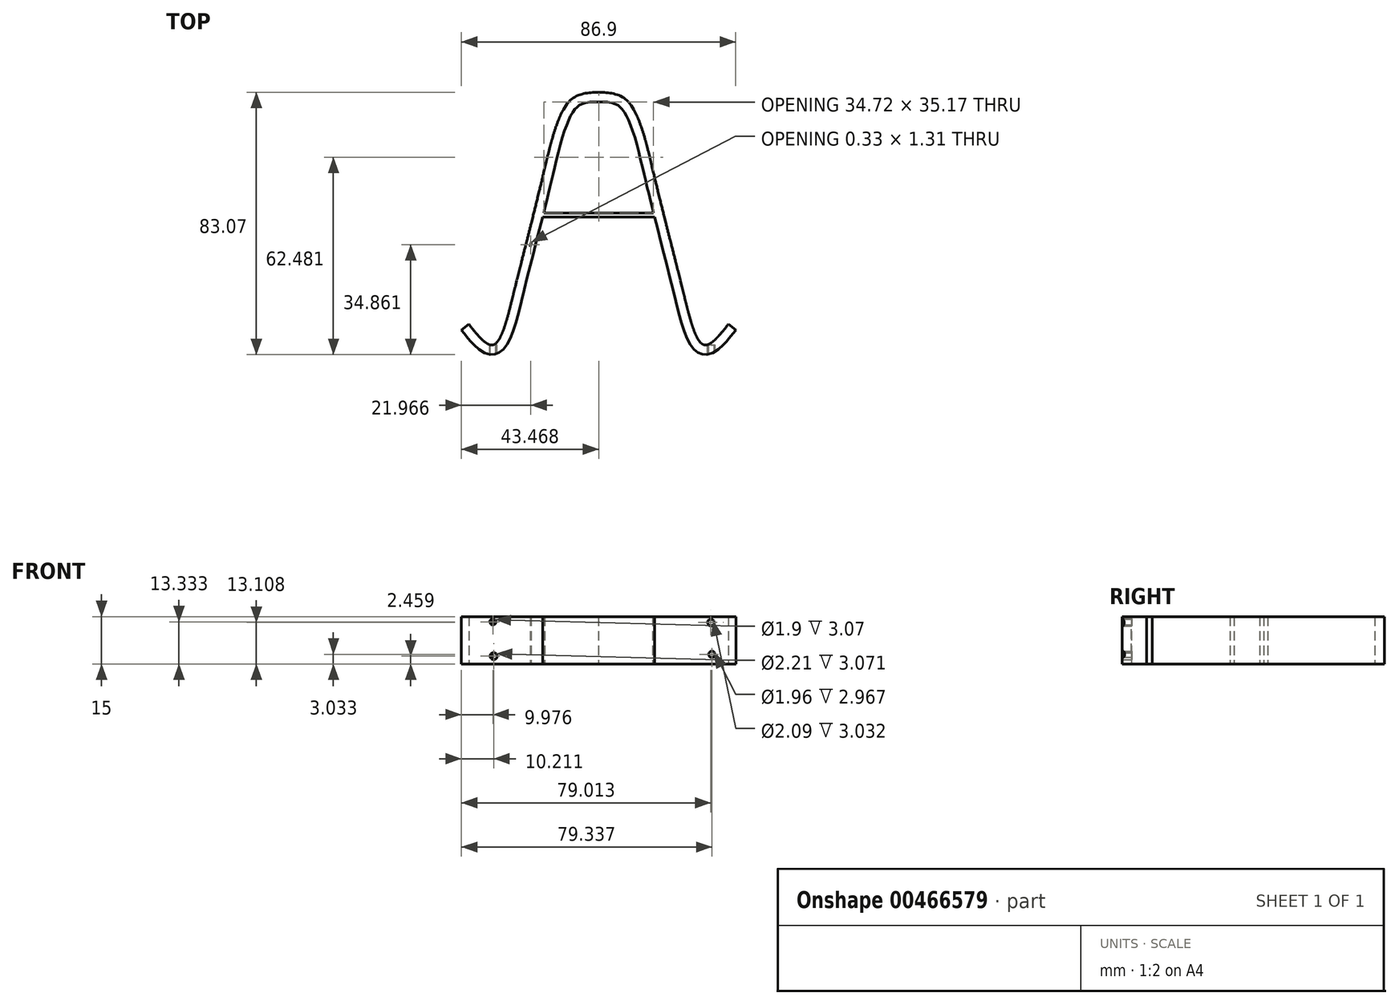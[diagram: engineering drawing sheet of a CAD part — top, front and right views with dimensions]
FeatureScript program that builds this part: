
annotation { "Feature Type Name" : "Feature", "Feature Type Description" : "" }
export const myFeature = defineFeature(function(context is Context, id is Id, definition is map)
    precondition{}
    {
        {
            var Q0;
            Q0=qCreatedBy(makeId("Top.planeOp"),FACE);
            var sketch = newSketch(context, id + "F0", { "sketchPlane" : qUnion([Q0])});
            skPoint(sketch, "E0", {"position": v(-40, 0) * mm});
            skPoint(sketch, "E1", {"position": v(40, 0) * mm});
            skPoint(sketch, "E2", {"position": v(0, 80) * mm});
            skFitSpline(sketch, "E3", {"points": [v(-41.08, 6.55) * mm, v(-38.1, 2.93) * mm, v(-33.42, 0) * mm, v(-26.81, 16.77) * mm, v(-17.66, 53.4) * mm, v(-8.92, 77.47) * mm, v(0, 80) * mm], "startDerivative": vector(27.62, -35.66) * mm, "endDerivative": vector(72.84, 2.27) * mm});
            skFitSpline(sketch, "E4.MirrorCS", {"points": [v(41.08, 6.55) * mm, v(38.1, 2.93) * mm, v(33.42, 0) * mm, v(26.81, 16.77) * mm, v(17.66, 53.4) * mm, v(8.92, 77.47) * mm, v(0, 80) * mm], "startDerivative": vector(-27.62, -35.66) * mm, "endDerivative": vector(-72.84, 2.27) * mm});
            skFitSpline(sketch, "E5.0", {"points": [v(-43.45, 4.7) * mm, v(-43.17, 4.34) * mm, v(-42.72, 3.77) * mm, v(-42.08, 2.96) * mm, v(-41.55, 2.32) * mm, v(-41.08, 1.76) * mm, v(-40.67, 1.3) * mm, v(-40.35, 0.93) * mm, v(-40, 0.56) * mm, v(-39.51, 0.04) * mm, v(-38.84, -0.64) * mm, v(-37.91, -1.45) * mm, v(-36.84, -2.2) * mm, v(-35.75, -2.74) * mm, v(-34.67, -3) * mm, v(-33.92, -3.07) * mm, v(-33.28, -3.03) * mm, v(-32.79, -2.94) * mm, v(-32.3, -2.8) * mm, v(-31.7, -2.57) * mm, v(-31.05, -2.18) * mm, v(-30.4, -1.65) * mm, v(-29.84, -1.07) * mm, v(-29.21, -0.25) * mm, v(-28.55, 0.83) * mm, v(-27.88, 2.26) * mm, v(-27.26, 3.82) * mm, v(-26.7, 5.5) * mm, v(-25.96, 7.91) * mm, v(-25.1, 11.16) * mm, v(-24.1, 15.28) * mm, v(-23.06, 19.44) * mm, v(-22, 23.66) * mm, v(-20.92, 27.91) * mm, v(-19.83, 32.2) * mm, v(-18.74, 36.51) * mm, v(-17.64, 40.85) * mm, v(-16.56, 45.2) * mm, v(-15.67, 48.82) * mm, v(-14.97, 51.71) * mm, v(-14.28, 54.6) * mm, v(-13.44, 58.18) * mm, v(-12.42, 62.28) * mm, v(-11.36, 66.07) * mm, v(-10.42, 68.88) * mm, v(-9.63, 70.85) * mm, v(-9.02, 72.17) * mm, v(-8.4, 73.31) * mm, v(-7.78, 74.26) * mm, v(-7.27, 74.88) * mm, v(-6.89, 75.27) * mm, v(-6.52, 75.6) * mm, v(-6.03, 75.93) * mm, v(-5.4, 76.25) * mm, v(-4.7, 76.5) * mm, v(-3.65, 76.75) * mm, v(-2.1, 76.93) * mm, v(-0.67, 76.98) * mm, v(0.1, 77) * mm]});
            skFitSpline(sketch, "E6.0", {"points": [v(43.45, 4.7) * mm, v(43.17, 4.34) * mm, v(42.72, 3.77) * mm, v(42.08, 2.96) * mm, v(41.55, 2.32) * mm, v(41.08, 1.76) * mm, v(40.67, 1.3) * mm, v(40.35, 0.93) * mm, v(40, 0.56) * mm, v(39.51, 0.04) * mm, v(38.84, -0.64) * mm, v(37.91, -1.45) * mm, v(36.84, -2.2) * mm, v(35.75, -2.74) * mm, v(34.67, -3) * mm, v(33.92, -3.07) * mm, v(33.28, -3.03) * mm, v(32.79, -2.94) * mm, v(32.3, -2.8) * mm, v(31.7, -2.57) * mm, v(31.05, -2.18) * mm, v(30.4, -1.65) * mm, v(29.84, -1.07) * mm, v(29.21, -0.25) * mm, v(28.55, 0.83) * mm, v(27.88, 2.26) * mm, v(27.26, 3.82) * mm, v(26.7, 5.5) * mm, v(25.96, 7.91) * mm, v(25.1, 11.16) * mm, v(24.1, 15.28) * mm, v(23.06, 19.44) * mm, v(22, 23.66) * mm, v(20.92, 27.91) * mm, v(19.83, 32.2) * mm, v(18.74, 36.51) * mm, v(17.64, 40.85) * mm, v(16.56, 45.2) * mm, v(15.67, 48.82) * mm, v(14.97, 51.71) * mm, v(14.28, 54.6) * mm, v(13.44, 58.18) * mm, v(12.42, 62.28) * mm, v(11.36, 66.07) * mm, v(10.42, 68.88) * mm, v(9.63, 70.85) * mm, v(9.02, 72.17) * mm, v(8.4, 73.31) * mm, v(7.78, 74.26) * mm, v(7.27, 74.88) * mm, v(6.89, 75.27) * mm, v(6.52, 75.6) * mm, v(6.03, 75.93) * mm, v(5.4, 76.25) * mm, v(4.7, 76.5) * mm, v(3.65, 76.75) * mm, v(2.1, 76.93) * mm, v(0.67, 76.98) * mm, v(-0.1, 77) * mm]});
            skLineSegment(sketch, "E7", {"start": v(-43.45, 4.7) * mm, "end": v(-41.08, 6.55) * mm});
            skLineSegment(sketch, "E8", {"start": v(43.45, 4.7) * mm, "end": v(41.08, 6.55) * mm});
            skLineSegment(sketch, "E9", {"start": v(-17.08, 43.11) * mm, "end": v(17.08, 43.11) * mm});
            skLineSegment(sketch, "E10", {"start": v(-17.73, 40.51) * mm, "end": v(17.73, 40.51) * mm});
            skFitSpline(sketch, "E11.trimOffspring", {"points": [v(-43.45, 4.7) * mm, v(-43.17, 4.34) * mm, v(-42.72, 3.77) * mm, v(-42.08, 2.96) * mm, v(-41.55, 2.32) * mm, v(-41.08, 1.76) * mm, v(-40.67, 1.3) * mm, v(-40.35, 0.93) * mm, v(-40, 0.56) * mm, v(-39.51, 0.04) * mm, v(-38.84, -0.64) * mm, v(-37.91, -1.45) * mm, v(-36.84, -2.2) * mm, v(-35.75, -2.74) * mm, v(-34.67, -3) * mm, v(-33.92, -3.07) * mm, v(-33.28, -3.03) * mm, v(-32.79, -2.94) * mm, v(-32.3, -2.8) * mm, v(-31.7, -2.57) * mm, v(-31.05, -2.18) * mm, v(-30.4, -1.65) * mm, v(-29.84, -1.07) * mm, v(-29.21, -0.25) * mm, v(-28.55, 0.83) * mm, v(-27.88, 2.26) * mm, v(-27.26, 3.82) * mm, v(-26.7, 5.5) * mm, v(-25.96, 7.91) * mm, v(-25.1, 11.16) * mm, v(-24.1, 15.28) * mm, v(-23.06, 19.44) * mm, v(-22, 23.66) * mm, v(-20.92, 27.91) * mm, v(-19.83, 32.2) * mm, v(-18.74, 36.51) * mm, v(-17.64, 40.85) * mm, v(-16.56, 45.2) * mm, v(-15.67, 48.82) * mm, v(-14.97, 51.71) * mm, v(-14.28, 54.6) * mm, v(-13.44, 58.18) * mm, v(-12.42, 62.28) * mm, v(-11.36, 66.07) * mm, v(-10.42, 68.88) * mm, v(-9.63, 70.85) * mm, v(-9.02, 72.17) * mm, v(-8.4, 73.31) * mm, v(-7.78, 74.26) * mm, v(-7.27, 74.88) * mm, v(-6.89, 75.27) * mm, v(-6.52, 75.6) * mm, v(-6.03, 75.93) * mm, v(-5.4, 76.25) * mm, v(-4.7, 76.5) * mm, v(-3.65, 76.75) * mm, v(-2.1, 76.93) * mm, v(-0.67, 76.98) * mm, v(0.1, 77) * mm]});
            skFitSpline(sketch, "E12.trimOffspring", {"points": [v(43.45, 4.7) * mm, v(43.17, 4.34) * mm, v(42.72, 3.77) * mm, v(42.08, 2.96) * mm, v(41.55, 2.32) * mm, v(41.08, 1.76) * mm, v(40.67, 1.3) * mm, v(40.35, 0.93) * mm, v(40, 0.56) * mm, v(39.51, 0.04) * mm, v(38.84, -0.64) * mm, v(37.91, -1.45) * mm, v(36.84, -2.2) * mm, v(35.75, -2.74) * mm, v(34.67, -3) * mm, v(33.92, -3.07) * mm, v(33.28, -3.03) * mm, v(32.79, -2.94) * mm, v(32.3, -2.8) * mm, v(31.7, -2.57) * mm, v(31.05, -2.18) * mm, v(30.4, -1.65) * mm, v(29.84, -1.07) * mm, v(29.21, -0.25) * mm, v(28.55, 0.83) * mm, v(27.88, 2.26) * mm, v(27.26, 3.82) * mm, v(26.7, 5.5) * mm, v(25.96, 7.91) * mm, v(25.1, 11.16) * mm, v(24.1, 15.28) * mm, v(23.06, 19.44) * mm, v(22, 23.66) * mm, v(20.92, 27.91) * mm, v(19.83, 32.2) * mm, v(18.74, 36.51) * mm, v(17.64, 40.85) * mm, v(16.56, 45.2) * mm, v(15.67, 48.82) * mm, v(14.97, 51.71) * mm, v(14.28, 54.6) * mm, v(13.44, 58.18) * mm, v(12.42, 62.28) * mm, v(11.36, 66.07) * mm, v(10.42, 68.88) * mm, v(9.63, 70.85) * mm, v(9.02, 72.17) * mm, v(8.4, 73.31) * mm, v(7.78, 74.26) * mm, v(7.27, 74.88) * mm, v(6.89, 75.27) * mm, v(6.52, 75.6) * mm, v(6.03, 75.93) * mm, v(5.4, 76.25) * mm, v(4.7, 76.5) * mm, v(3.65, 76.75) * mm, v(2.1, 76.93) * mm, v(0.67, 76.98) * mm, v(-0.1, 77) * mm]});
            skFitSpline(sketch, "E13.0", {"points": [v(-42.27, 5.63) * mm, v(-41.98, 5.26) * mm, v(-41.54, 4.7) * mm, v(-40.91, 3.9) * mm, v(-40.4, 3.28) * mm, v(-39.85, 2.63) * mm, v(-39.24, 1.95) * mm, v(-38.56, 1.2) * mm, v(-37.8, 0.45) * mm, v(-36.98, -0.28) * mm, v(-36.07, -0.91) * mm, v(-35.2, -1.33) * mm, v(-34.42, -1.52) * mm, v(-33.79, -1.57) * mm, v(-33.23, -1.51) * mm, v(-32.8, -1.38) * mm, v(-32.38, -1.22) * mm, v(-31.91, -0.95) * mm, v(-31.26, -0.41) * mm, v(-30.58, 0.4) * mm, v(-29.88, 1.53) * mm, v(-29.26, 2.85) * mm, v(-28.67, 4.33) * mm, v(-28.12, 5.96) * mm, v(-27.41, 8.31) * mm, v(-26.56, 11.53) * mm, v(-25.55, 15.64) * mm, v(-24.52, 19.8) * mm, v(-23.46, 24.03) * mm, v(-22.38, 28.28) * mm, v(-20.92, 34) * mm, v(-19.46, 39.77) * mm, v(-18.02, 45.55) * mm, v(-17.13, 49.17) * mm, v(-16.43, 52.06) * mm, v(-15.74, 54.95) * mm, v(-14.9, 58.53) * mm, v(-13.87, 62.65) * mm, v(-12.8, 66.5) * mm, v(-11.64, 69.96) * mm, v(-10.6, 72.42) * mm, v(-9.7, 74.07) * mm, v(-9, 75.14) * mm, v(-8.28, 76.02) * mm, v(-7.56, 76.7) * mm, v(-6.8, 77.22) * mm, v(-5.72, 77.77) * mm, v(-4.23, 78.2) * mm, v(-2.2, 78.43) * mm, v(-0.71, 78.48) * mm, v(0.05, 78.5) * mm]});
            skFitSpline(sketch, "E14.0", {"points": [v(42.27, 5.63) * mm, v(41.98, 5.26) * mm, v(41.54, 4.7) * mm, v(40.91, 3.9) * mm, v(40.4, 3.28) * mm, v(39.85, 2.63) * mm, v(39.24, 1.95) * mm, v(38.56, 1.2) * mm, v(37.8, 0.45) * mm, v(36.98, -0.28) * mm, v(36.07, -0.91) * mm, v(35.2, -1.33) * mm, v(34.42, -1.52) * mm, v(33.79, -1.57) * mm, v(33.23, -1.51) * mm, v(32.8, -1.38) * mm, v(32.38, -1.22) * mm, v(31.91, -0.95) * mm, v(31.26, -0.41) * mm, v(30.58, 0.4) * mm, v(29.88, 1.53) * mm, v(29.26, 2.85) * mm, v(28.67, 4.33) * mm, v(28.12, 5.96) * mm, v(27.41, 8.31) * mm, v(26.56, 11.53) * mm, v(25.55, 15.64) * mm, v(24.52, 19.8) * mm, v(23.46, 24.03) * mm, v(22.38, 28.28) * mm, v(20.92, 34) * mm, v(19.46, 39.77) * mm, v(18.02, 45.55) * mm, v(17.13, 49.17) * mm, v(16.43, 52.06) * mm, v(15.74, 54.95) * mm, v(14.9, 58.53) * mm, v(13.87, 62.65) * mm, v(12.8, 66.5) * mm, v(11.64, 69.96) * mm, v(10.6, 72.42) * mm, v(9.7, 74.07) * mm, v(9, 75.14) * mm, v(8.28, 76.02) * mm, v(7.56, 76.7) * mm, v(6.8, 77.22) * mm, v(5.72, 77.77) * mm, v(4.23, 78.2) * mm, v(2.2, 78.43) * mm, v(0.71, 78.48) * mm, v(-0.05, 78.5) * mm]});
            skLineSegment(sketch, "E15", {"start": v(-17.34, 41.82) * mm, "end": v(17.38, 41.82) * mm});
            skLineSegment(sketch, "E16", {"start": v(-17.34, 41.82) * mm, "end": v(-17.08, 43.11) * mm});
            skLineSegment(sketch, "E17", {"start": v(17.38, 41.82) * mm, "end": v(17.08, 43.11) * mm});
            skLineSegment(sketch, "E18", {"start": v(-41.43, 4.56) * mm, "end": v(-40.22, 5.43) * mm});
            skLineSegment(sketch, "E19", {"start": v(-39.27, 1.98) * mm, "end": v(-38.1, 2.93) * mm});
            skLineSegment(sketch, "E20", {"start": v(-38.36, 1) * mm, "end": v(-37.3, 2.06) * mm});
            skLineSegment(sketch, "E21", {"start": v(-35.26, 0.39) * mm, "end": v(-35.26, -1.27) * mm});
            skLineSegment(sketch, "E22", {"start": v(-33.88, -0.05) * mm, "end": v(-33.88, -1.55) * mm});
            skLineSegment(sketch, "E23", {"start": v(-31.9, 1.18) * mm, "end": v(-30.54, 0.5) * mm});
            skLineSegment(sketch, "E24", {"start": v(-30.54, 0.5) * mm, "end": v(-30.58, 0.53) * mm});
            skLineSegment(sketch, "E25", {"start": v(-31.16, 2.38) * mm, "end": v(-29.77, 1.8) * mm});
            skLineSegment(sketch, "E26", {"start": v(-29.77, 5.78) * mm, "end": v(-28.42, 5.1) * mm});
            skLineSegment(sketch, "E27", {"start": v(-29.26, 7.4) * mm, "end": v(-27.85, 6.85) * mm});
            skLineSegment(sketch, "E28", {"start": v(-28.1, 11.56) * mm, "end": v(-26.72, 10.96) * mm});
            skLineSegment(sketch, "E29", {"start": v(-27.73, 13.05) * mm, "end": v(-26.34, 12.42) * mm});
            skLineSegment(sketch, "E30", {"start": v(-26.37, 18.58) * mm, "end": v(-24.97, 17.95) * mm});
            skLineSegment(sketch, "E31", {"start": v(-25.89, 20.49) * mm, "end": v(-24.47, 20) * mm});
            skLineSegment(sketch, "E32", {"start": v(-24.84, 24.66) * mm, "end": v(-23.45, 24.04) * mm});
            skLineSegment(sketch, "E33", {"start": v(-24.47, 26.14) * mm, "end": v(-23.08, 25.51) * mm});
            skLineSegment(sketch, "E34", {"start": v(-23.08, 25.51) * mm, "end": v(-22.95, 25.96) * mm});
            skLineSegment(sketch, "E35.MirrorCS", {"start": v(41.43, 4.56) * mm, "end": v(40.22, 5.43) * mm});
            skLineSegment(sketch, "E36.MirrorCS", {"start": v(39.27, 1.98) * mm, "end": v(38.1, 2.93) * mm});
            skLineSegment(sketch, "E37.MirrorCS", {"start": v(38.36, 1) * mm, "end": v(37.3, 2.06) * mm});
            skLineSegment(sketch, "E38.MirrorCS", {"start": v(35.26, 0.39) * mm, "end": v(35.26, -1.27) * mm});
            skLineSegment(sketch, "E39.MirrorCS", {"start": v(33.88, -0.05) * mm, "end": v(33.88, -1.55) * mm});
            skLineSegment(sketch, "E40.MirrorCS", {"start": v(31.9, 1.18) * mm, "end": v(30.54, 0.5) * mm});
            skLineSegment(sketch, "E41.MirrorCS", {"start": v(31.16, 2.38) * mm, "end": v(29.77, 1.8) * mm});
            skLineSegment(sketch, "E42.MirrorCS", {"start": v(29.77, 5.78) * mm, "end": v(28.42, 5.1) * mm});
            skLineSegment(sketch, "E43.MirrorCS", {"start": v(29.26, 7.4) * mm, "end": v(27.85, 6.85) * mm});
            skLineSegment(sketch, "E44.MirrorCS", {"start": v(28.1, 11.56) * mm, "end": v(26.72, 10.96) * mm});
            skLineSegment(sketch, "E45.MirrorCS", {"start": v(27.73, 13.05) * mm, "end": v(26.34, 12.42) * mm});
            skLineSegment(sketch, "E46.MirrorCS", {"start": v(26.37, 18.58) * mm, "end": v(24.97, 17.95) * mm});
            skLineSegment(sketch, "E47.MirrorCS", {"start": v(25.89, 20.49) * mm, "end": v(24.47, 20) * mm});
            skLineSegment(sketch, "E48.MirrorCS", {"start": v(24.47, 26.14) * mm, "end": v(23.08, 25.51) * mm});
            skLineSegment(sketch, "E49.MirrorCS", {"start": v(24.84, 24.66) * mm, "end": v(23.45, 24.04) * mm});
            skLineSegment(sketch, "E50", {"start": v(-23.04, 31.76) * mm, "end": v(-21.65, 31.14) * mm});
            skLineSegment(sketch, "E51", {"start": v(-21.65, 31.14) * mm, "end": v(-21.3, 32.54) * mm});
            skLineSegment(sketch, "E52", {"start": v(-21.3, 32.54) * mm, "end": v(-22.67, 33.23) * mm});
            skLineSegment(sketch, "E53", {"start": v(-21.3, 38.64) * mm, "end": v(-19.84, 38.27) * mm});
            skLineSegment(sketch, "E54", {"start": v(-20.88, 40.28) * mm, "end": v(-19.45, 39.8) * mm});
            skLineSegment(sketch, "E55", {"start": v(-19.3, 46.58) * mm, "end": v(-17.9, 46) * mm});
            skLineSegment(sketch, "E56", {"start": v(-18.8, 48.7) * mm, "end": v(-17.4, 48.1) * mm});
            skLineSegment(sketch, "E57", {"start": v(-17.4, 54.51) * mm, "end": v(-15.99, 53.92) * mm});
            skLineSegment(sketch, "E58", {"start": v(-16.9, 56.58) * mm, "end": v(-15.5, 55.99) * mm});
            skLineSegment(sketch, "E59", {"start": v(-15.36, 62.82) * mm, "end": v(-13.96, 62.24) * mm});
            skLineSegment(sketch, "E60", {"start": v(-14.66, 65.38) * mm, "end": v(-13.27, 64.8) * mm});
            skPoint(sketch, "E60.startSnap0", {"position": v(-14.66, 62.53) * mm});
            skLineSegment(sketch, "E61", {"start": v(-13.27, 64.8) * mm, "end": v(-13.38, 64.48) * mm});
            skLineSegment(sketch, "E62", {"start": v(-12.67, 71.32) * mm, "end": v(-11.4, 70.47) * mm});
            skLineSegment(sketch, "E63", {"start": v(-11.92, 73.04) * mm, "end": v(-10.6, 72.31) * mm});
            skLineSegment(sketch, "E64.MirrorCS", {"start": v(21.3, 32.54) * mm, "end": v(22.67, 33.23) * mm});
            skLineSegment(sketch, "E65.MirrorCS", {"start": v(23.04, 31.76) * mm, "end": v(21.65, 31.14) * mm});
            skLineSegment(sketch, "E66.MirrorCS", {"start": v(21.3, 38.64) * mm, "end": v(19.84, 38.27) * mm});
            skLineSegment(sketch, "E67.MirrorCS", {"start": v(20.88, 40.28) * mm, "end": v(19.45, 39.8) * mm});
            skLineSegment(sketch, "E68.MirrorCS", {"start": v(19.3, 46.58) * mm, "end": v(17.9, 46) * mm});
            skLineSegment(sketch, "E69.MirrorCS", {"start": v(18.8, 48.7) * mm, "end": v(17.4, 48.1) * mm});
            skLineSegment(sketch, "E70.MirrorCS", {"start": v(17.4, 54.51) * mm, "end": v(15.99, 53.92) * mm});
            skLineSegment(sketch, "E71.MirrorCS", {"start": v(16.9, 56.58) * mm, "end": v(15.5, 55.99) * mm});
            skLineSegment(sketch, "E72.MirrorCS", {"start": v(15.36, 62.82) * mm, "end": v(13.96, 62.24) * mm});
            skLineSegment(sketch, "E73.MirrorCS", {"start": v(14.66, 65.38) * mm, "end": v(13.27, 64.8) * mm});
            skLineSegment(sketch, "E74.MirrorCS", {"start": v(12.67, 71.32) * mm, "end": v(11.4, 70.47) * mm});
            skLineSegment(sketch, "E75.MirrorCS", {"start": v(11.92, 73.04) * mm, "end": v(10.6, 72.31) * mm});
            skFitSpline(sketch, "E76.trimOffspring", {"points": [v(41.08, 6.55) * mm, v(38.1, 2.93) * mm, v(33.42, 0) * mm, v(26.81, 16.77) * mm, v(17.66, 53.4) * mm, v(8.92, 77.47) * mm, v(0, 80) * mm], "startDerivative": vector(-27.62, -35.66) * mm, "endDerivative": vector(-72.84, 2.27) * mm});
            skLineSegment(sketch, "E77", {"start": v(41.08, 6.55) * mm, "end": v(40.22, 5.43) * mm});
            skPoint(sketch, "E78.end.orphan", {"position": v(-8.08, 76.2) * mm});
            skPoint(sketch, "E79.end.orphan", {"position": v(-6.97, 77.1) * mm});
            skPoint(sketch, "E79.start.orphan", {"position": v(-7.72, 78.4) * mm});
            skPoint(sketch, "E80.end.orphan", {"position": v(-1.06, 78.46) * mm});
            skPoint(sketch, "E81.MirrorCS.end.orphan", {"position": v(1.06, 78.46) * mm});
            skPoint(sketch, "E82.MirrorCS.end.orphan", {"position": v(6.97, 77.1) * mm});
            skPoint(sketch, "E83.MirrorCS.end.orphan", {"position": v(8.08, 76.2) * mm});
            skPoint(sketch, "E84.trimOffspring.end.orphan", {"position": v(7.72, 78.4) * mm});
            skSolve(sketch);
        }
        {
            var Q0;
            Q0 = qSketchRegion(id + "F0", true);
            extrude(context, id + "F1", {"entities" : qUnion([Q0]), "depth" : 15 * mm});
        }
        {
            var Q0;
            Q0=qCreatedBy(makeId("Front.planeOp"),FACE);
            var sketch = newSketch(context, id + "F2", { "sketchPlane" : qUnion([Q0])});
            skCircle(sketch, "E85", {"center": v(-33.47, 13.33) * mm, "radius": 0.95 * mm});
            skCircle(sketch, "E86", {"center": v(-33.24, 2.46) * mm, "radius": 1.1 * mm});
            skCircle(sketch, "E87", {"center": v(35.56, 13.1) * mm, "radius": 1.05 * mm});
            skCircle(sketch, "E88", {"center": v(35.89, 3.03) * mm, "radius": 0.98 * mm});
            skSolve(sketch);
        }
        {
            var Q0;
            Q0 = qSketchRegion(id + "F2", true);
            extrude(context, id + "F3", {"entities" : qUnion([Q0]), "operationType" : NewBodyOperationType.REMOVE, "depth" : 4 * mm});
        }
    });
